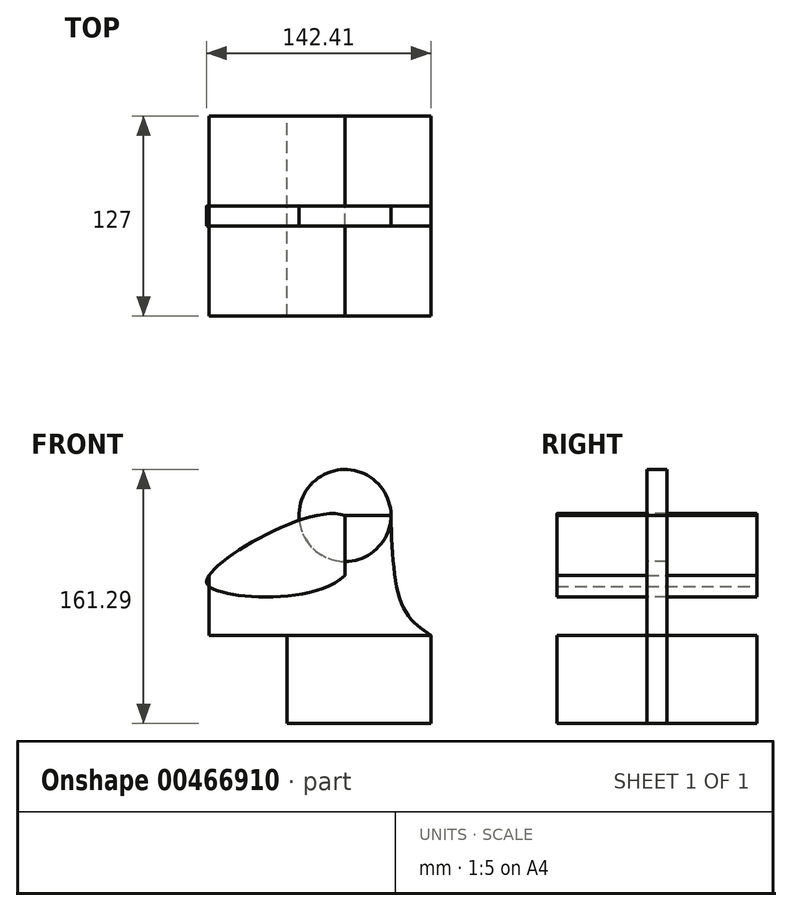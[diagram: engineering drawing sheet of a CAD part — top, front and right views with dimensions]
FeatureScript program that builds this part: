
annotation { "Feature Type Name" : "Feature", "Feature Type Description" : "" }
export const myFeature = defineFeature(function(context is Context, id is Id, definition is map)
    precondition{}
    {
        {
            var Q0;
            Q0=qCreatedBy(makeId("Front.planeOp"),FACE);
            var sketch = newSketch(context, id + "F0", { "sketchPlane" : qUnion([Q0])});
            skLineSegment(sketch, "E0.bottom", {"start": v(-62.82, 25.48) * mm, "end": v(23.54, 25.48) * mm});
            skLineSegment(sketch, "E0.top", {"start": v(-62.82, -12.62) * mm, "end": v(23.54, -12.62) * mm});
            skLineSegment(sketch, "E0.left", {"start": v(-62.82, 25.48) * mm, "end": v(-62.82, -12.62) * mm});
            skLineSegment(sketch, "E0.right", {"start": v(23.54, 25.48) * mm, "end": v(23.54, -12.62) * mm});
            skLineSegment(sketch, "E1.bottom", {"start": v(-13.33, -12.62) * mm, "end": v(78.11, -12.62) * mm});
            skLineSegment(sketch, "E1.top", {"start": v(-13.33, -68.5) * mm, "end": v(78.11, -68.5) * mm});
            skLineSegment(sketch, "E1.left", {"start": v(-13.33, -12.62) * mm, "end": v(-13.33, -68.5) * mm});
            skLineSegment(sketch, "E1.right", {"start": v(78.11, -12.62) * mm, "end": v(78.11, -68.5) * mm});
            skLineSegment(sketch, "E2.bottom", {"start": v(52.75, -12.62) * mm, "end": v(23.54, -12.62) * mm});
            skLineSegment(sketch, "E2.top", {"start": v(52.75, 63.58) * mm, "end": v(23.54, 63.58) * mm});
            skLineSegment(sketch, "E2.left", {"start": v(52.75, -12.62) * mm, "end": v(52.75, 63.58) * mm});
            skLineSegment(sketch, "E2.right", {"start": v(23.54, -12.62) * mm, "end": v(23.54, 63.58) * mm});
            skFitSpline(sketch, "E3", {"points": [v(-62.82, 25.48) * mm, v(23.54, 63.58) * mm, v(23.54, 25.48) * mm, v(-58.15, 16.12) * mm, v(-62.82, 25.48) * mm]});
            skFitSpline(sketch, "E4", {"points": [v(52.75, 63.58) * mm, v(60.65, 4.98) * mm, v(78.11, -12.62) * mm], "startDerivative": vector(3.47, -112.26) * mm, "endDerivative": vector(50.61, -34.6) * mm});
            skSolve(sketch);
        }
        {
            var Q0;
            {var subQ0=sQuery(id+"F0.wireOp",EDGE,"E0.bottom");Q0=makeQuery(id+"F0.imprint","IMPRINT",FACE,{"disambiguationData":[TD([[makeQuery(id+"F0.imprint","IMPRINT",EDGE,{"derivedFrom":subQ0}),1.0]])]});}
            var Q1;
            {var subQ0=sQuery(id+"F0.wireOp",EDGE,"E0.bottom");Q1=makeQuery(id+"F0.imprint","IMPRINT",FACE,{"disambiguationData":[TD([[makeQuery(id+"F0.imprint","IMPRINT",EDGE,{"derivedFrom":subQ0}),-1.0]])]});}
            var Q2;
            Q2=makeQuery(id+"F0.imprint","IMPRINT",FACE,{"disambiguationData":[TD([[makeQuery(id+"F0.imprint","IMPRINT",EDGE,{"derivedFrom":sQuery(id+"F0.wireOp",EDGE,"E1.top")}),1.0]])]});
            extrude(context, id + "F1", {"entities" : qUnion([Q0, Q1, Q2]), "endBound" : BoundingType.SYMMETRIC, "depth" : 127 * mm});
        }
        {
            var Q0;
            Q0 = qSketchRegion(id + "F0", true);
            extrude(context, id + "F2", {"entities" : qUnion([Q0]), "endBound" : BoundingType.SYMMETRIC, "depth" : 12.7 * mm});
        }
        {
            var Q0;
            Q0=makeQuery(id+"F2.opExtrude","SWEPT_FACE",FACE,{"disambiguationData":[OSD([sQuery(id+"F0.wireOp",EDGE,"E2.top")])]});
            var Q1;
            Q1=makeQuery(id+"F1.opExtrude","SWEPT_EDGE",EDGE,{"disambiguationData":[OSD([sQuery(id+"F0.wireOp",EDGE,"E2.top"),sQuery(id+"F0.wireOp",EDGE,"E2.right"),sQuery(id+"F0.wireOp",EDGE,"E3")])]});
            revolve(context, id + "F3", {"entities" : qUnion([Q0]), "axis" : qUnion([Q1]), "revolveType" : RevolveType.FULL});
        }
    });
